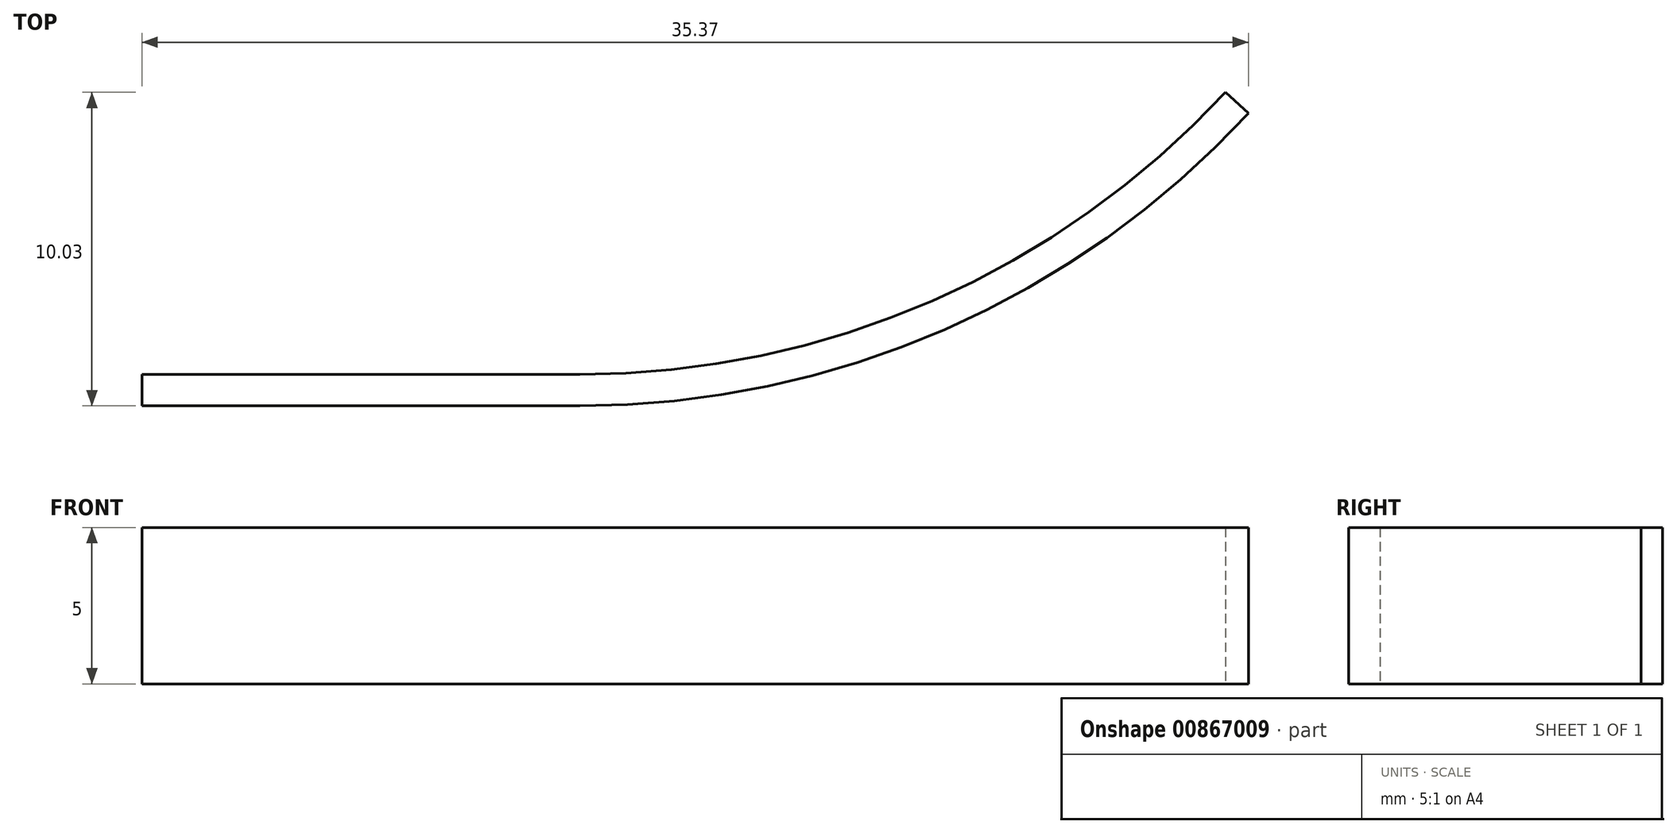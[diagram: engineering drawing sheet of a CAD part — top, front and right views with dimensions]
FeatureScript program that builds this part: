
annotation { "Feature Type Name" : "Feature", "Feature Type Description" : "" }
export const myFeature = defineFeature(function(context is Context, id is Id, definition is map)
    precondition{}
    {
        {
            var Q0;
            Q0=qCreatedBy(makeId("Top.planeOp"),FACE);
            var sketch = newSketch(context, id + "F0", { "sketchPlane" : qUnion([Q0])});
            skLineSegment(sketch, "E0", {"start": v(0, 0) * mm, "end": v(14, 0) * mm});
            skArc(sketch, "E1", {"start": v(14, 0) * mm, "mid": v(25.46, 2.4) * mm, "end": v(35, 9.2) * mm});
            skSolve(sketch);
        }
        {
            var Q0;
            Q0=qCreatedBy(makeId("Right.planeOp"),FACE);
            var sketch = newSketch(context, id + "F1", { "sketchPlane" : qUnion([Q0])});
            skLineSegment(sketch, "E2.bottom", {"start": v(0.5, 2.5) * mm, "end": v(-0.5, 2.5) * mm});
            skLineSegment(sketch, "E2.top", {"start": v(0.5, -2.5) * mm, "end": v(-0.5, -2.5) * mm});
            skLineSegment(sketch, "E2.left", {"start": v(0.5, 2.5) * mm, "end": v(0.5, -2.5) * mm});
            skLineSegment(sketch, "E2.right", {"start": v(-0.5, 2.5) * mm, "end": v(-0.5, -2.5) * mm});
            skPoint(sketch, "E2.middle", {"position": v(0, 0) * mm});
            skSolve(sketch);
        }
        {
            var Q0;
            Q0=makeQuery(id+"F1.imprint","IMPRINT",FACE,{"disambiguationData":[TD([[makeQuery(id+"F1.imprint","IMPRINT",EDGE,{"derivedFrom":sQuery(id+"F1.wireOp",EDGE,"E2.bottom")}),1.0]])]});
            var Q1;
            Q1=sQuery(id+"F0.wireOp",EDGE,"E0");
            var Q2;
            Q2=sQuery(id+"F0.wireOp",EDGE,"E1");
            sweep(context, id + "F2", {"profiles" : qUnion([Q0]), "path" : qUnion([Q1, Q2])});
        }
    });
